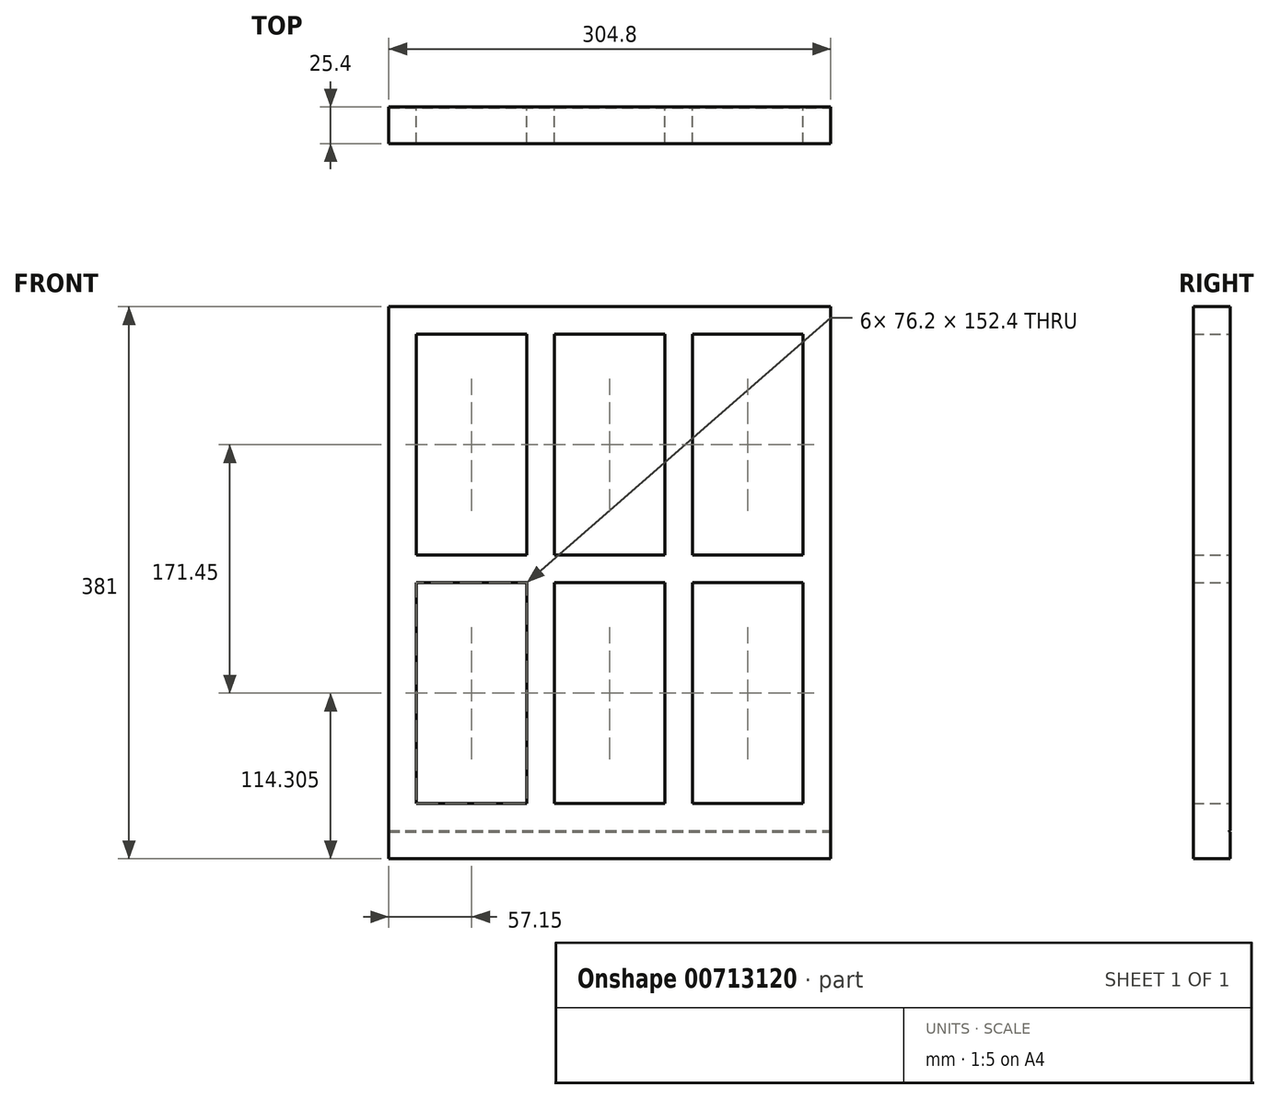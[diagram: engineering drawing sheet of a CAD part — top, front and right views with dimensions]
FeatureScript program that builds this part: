
annotation { "Feature Type Name" : "Feature", "Feature Type Description" : "" }
export const myFeature = defineFeature(function(context is Context, id is Id, definition is map)
    precondition{}
    {
        {
            var Q0;
            Q0=qCreatedBy(makeId("Front.planeOp"),FACE);
            var sketch = newSketch(context, id + "F0", { "sketchPlane" : qUnion([Q0])});
            skLineSegment(sketch, "E0.bottom", {"start": v(-152.4, 208.26) * mm, "end": v(152.4, 208.26) * mm});
            skLineSegment(sketch, "E0.left", {"start": v(-152.4, 208.26) * mm, "end": v(-152.4, -172.74) * mm});
            skLineSegment(sketch, "E0.right", {"start": v(152.4, 208.26) * mm, "end": v(152.4, -172.74) * mm});
            skLineSegment(sketch, "E1.bottom", {"start": v(-133.35, 189.21) * mm, "end": v(-57.15, 189.21) * mm});
            skLineSegment(sketch, "E1.top", {"start": v(-133.35, 36.81) * mm, "end": v(-57.15, 36.81) * mm});
            skLineSegment(sketch, "E1.left", {"start": v(-133.35, 189.21) * mm, "end": v(-133.35, 36.81) * mm});
            skLineSegment(sketch, "E1.right", {"start": v(-57.15, 189.21) * mm, "end": v(-57.15, 36.81) * mm});
            skPoint(sketch, "E1.middle", {"position": v(-95.25, 113.01) * mm});
            skLineSegment(sketch, "E2.direction1", {"start": v(-133.35, 36.81) * mm, "end": v(-38.1, 36.81) * mm, "construction": true});
            skLineSegment(sketch, "E2.direction2", {"start": v(-133.35, 36.81) * mm, "end": v(-133.35, 30.46) * mm, "construction": true});
            skLineSegment(sketch, "E3.0.1.0", {"start": v(-57.15, 17.76) * mm, "end": v(-57.15, -134.64) * mm});
            skLineSegment(sketch, "E3.0.1.1", {"start": v(-133.35, 17.76) * mm, "end": v(-133.35, -134.64) * mm});
            skPoint(sketch, "E3.0.1.2", {"position": v(-95.25, -74.95) * mm});
            skLineSegment(sketch, "E3.0.1.3", {"start": v(-133.35, 17.76) * mm, "end": v(-57.15, 17.76) * mm});
            skLineSegment(sketch, "E3.0.1.5", {"start": v(-133.35, -134.64) * mm, "end": v(-57.15, -134.64) * mm});
            skLineSegment(sketch, "E3.1.0.0", {"start": v(38.1, 189.21) * mm, "end": v(38.1, 36.81) * mm});
            skLineSegment(sketch, "E3.1.0.1", {"start": v(-38.1, 189.21) * mm, "end": v(-38.1, 36.81) * mm});
            skPoint(sketch, "E3.1.0.2", {"position": v(0, 113.01) * mm});
            skLineSegment(sketch, "E3.1.0.3", {"start": v(-38.1, 189.21) * mm, "end": v(38.1, 189.21) * mm});
            skLineSegment(sketch, "E3.1.0.4", {"start": v(-38.1, 36.81) * mm, "end": v(57.15, 36.81) * mm, "construction": true});
            skLineSegment(sketch, "E3.1.0.5", {"start": v(-38.1, 36.81) * mm, "end": v(38.1, 36.81) * mm});
            skLineSegment(sketch, "E3.1.0.6", {"start": v(-38.1, 36.81) * mm, "end": v(-38.1, 26.47) * mm, "construction": true});
            skLineSegment(sketch, "E3.1.1.0", {"start": v(38.1, 17.76) * mm, "end": v(38.1, -134.64) * mm});
            skLineSegment(sketch, "E3.1.1.1", {"start": v(-38.1, 17.76) * mm, "end": v(-38.1, -134.64) * mm});
            skPoint(sketch, "E3.1.1.2", {"position": v(0, -74.95) * mm});
            skLineSegment(sketch, "E3.1.1.3", {"start": v(-38.1, 17.76) * mm, "end": v(38.1, 17.76) * mm});
            skLineSegment(sketch, "E3.1.1.4", {"start": v(-38.1, -134.64) * mm, "end": v(38.1, -134.64) * mm, "construction": true});
            skLineSegment(sketch, "E3.1.1.5", {"start": v(-38.1, -134.64) * mm, "end": v(38.1, -134.64) * mm});
            skLineSegment(sketch, "E3.2.0.0", {"start": v(133.35, 189.21) * mm, "end": v(133.35, 36.81) * mm});
            skLineSegment(sketch, "E3.2.0.1", {"start": v(57.15, 189.21) * mm, "end": v(57.15, 36.81) * mm});
            skPoint(sketch, "E3.2.0.2", {"position": v(95.25, 113.01) * mm});
            skLineSegment(sketch, "E3.2.0.3", {"start": v(57.15, 189.21) * mm, "end": v(133.35, 189.21) * mm});
            skLineSegment(sketch, "E3.2.0.4", {"start": v(57.15, 36.81) * mm, "end": v(152.4, 36.81) * mm, "construction": true});
            skLineSegment(sketch, "E3.2.0.5", {"start": v(57.15, 36.81) * mm, "end": v(133.35, 36.81) * mm});
            skLineSegment(sketch, "E3.2.0.6", {"start": v(57.15, 36.81) * mm, "end": v(57.15, 30.46) * mm, "construction": true});
            skLineSegment(sketch, "E3.2.1.0", {"start": v(133.35, 17.76) * mm, "end": v(133.35, -134.64) * mm});
            skLineSegment(sketch, "E3.2.1.1", {"start": v(57.15, 17.76) * mm, "end": v(57.15, -134.64) * mm});
            skPoint(sketch, "E3.2.1.2", {"position": v(95.25, -74.95) * mm});
            skLineSegment(sketch, "E3.2.1.3", {"start": v(57.15, 17.76) * mm, "end": v(133.35, 17.76) * mm});
            skLineSegment(sketch, "E3.2.1.4", {"start": v(57.15, -134.64) * mm, "end": v(133.35, -134.64) * mm, "construction": true});
            skLineSegment(sketch, "E3.2.1.5", {"start": v(57.15, -134.64) * mm, "end": v(133.35, -134.64) * mm});
            skLineSegment(sketch, "E3.direction2", {"start": v(-133.35, 30.46) * mm, "end": v(-133.35, -134.64) * mm, "construction": true});
            skLineSegment(sketch, "E4", {"start": v(-152.4, -153.69) * mm, "end": v(152.4, -153.69) * mm});
            skLineSegment(sketch, "E5", {"start": v(152.4, -172.74) * mm, "end": v(-152.4, -172.74) * mm});
            skSolve(sketch);
        }
        {
            var Q0;
            Q0 = qSketchRegion(id + "F0", true);
            extrude(context, id + "F1", {"entities" : qUnion([Q0]), "depth" : 25.4 * mm, "offsetDistance" : 25.4 * mm});
        }
        {
            var Q0;
            Q0=makeQuery(id+"F1.opExtrude","SWEPT_FACE",FACE,{"disambiguationData":[OSD([sQuery(id+"F0.wireOp",EDGE,"E0.right")])]});
            var sketch = newSketch(context, id + "F2", { "sketchPlane" : qUnion([Q0])});
            skCircle(sketch, "E6", {"center": v(0, -153.67) * mm, "radius": 0.53 * mm});
            skSolve(sketch);
        }
        {
            var Q0;
            {var subQ0=sQuery(id+"F2.wireOp",EDGE,"E6");var subQ1=makeQuery(id+"F1.opExtrude","CAP_EDGE",EDGE,{"disambiguationData":[OSD([sQuery(id+"F0.wireOp",EDGE,"E0.right")])],"isStart":true});var subQ2=makeQuery(id+"F2.imprint","INTERSECT",VERTEX,{"disambiguationData":[OD(0.0)],"derivedFrom":[subQ1,subQ0]});Q0=makeQuery(id+"F2.imprint","IMPRINT",FACE,{"disambiguationData":[TD([[makeQuery(id+"F2.imprint","IMPRINT",EDGE,{"disambiguationData":[TD([[subQ2,-1.0]])],"derivedFrom":subQ0}),1.0]])]});}
            extrude(context, id + "F3", {"entities" : qUnion([Q0]), "operationType" : NewBodyOperationType.REMOVE, "endBound" : BoundingType.THROUGH_ALL, "oppositeDirection" : true, "depth" : 25.4 * mm, "offsetDistance" : 25.4 * mm});
        }
    });
